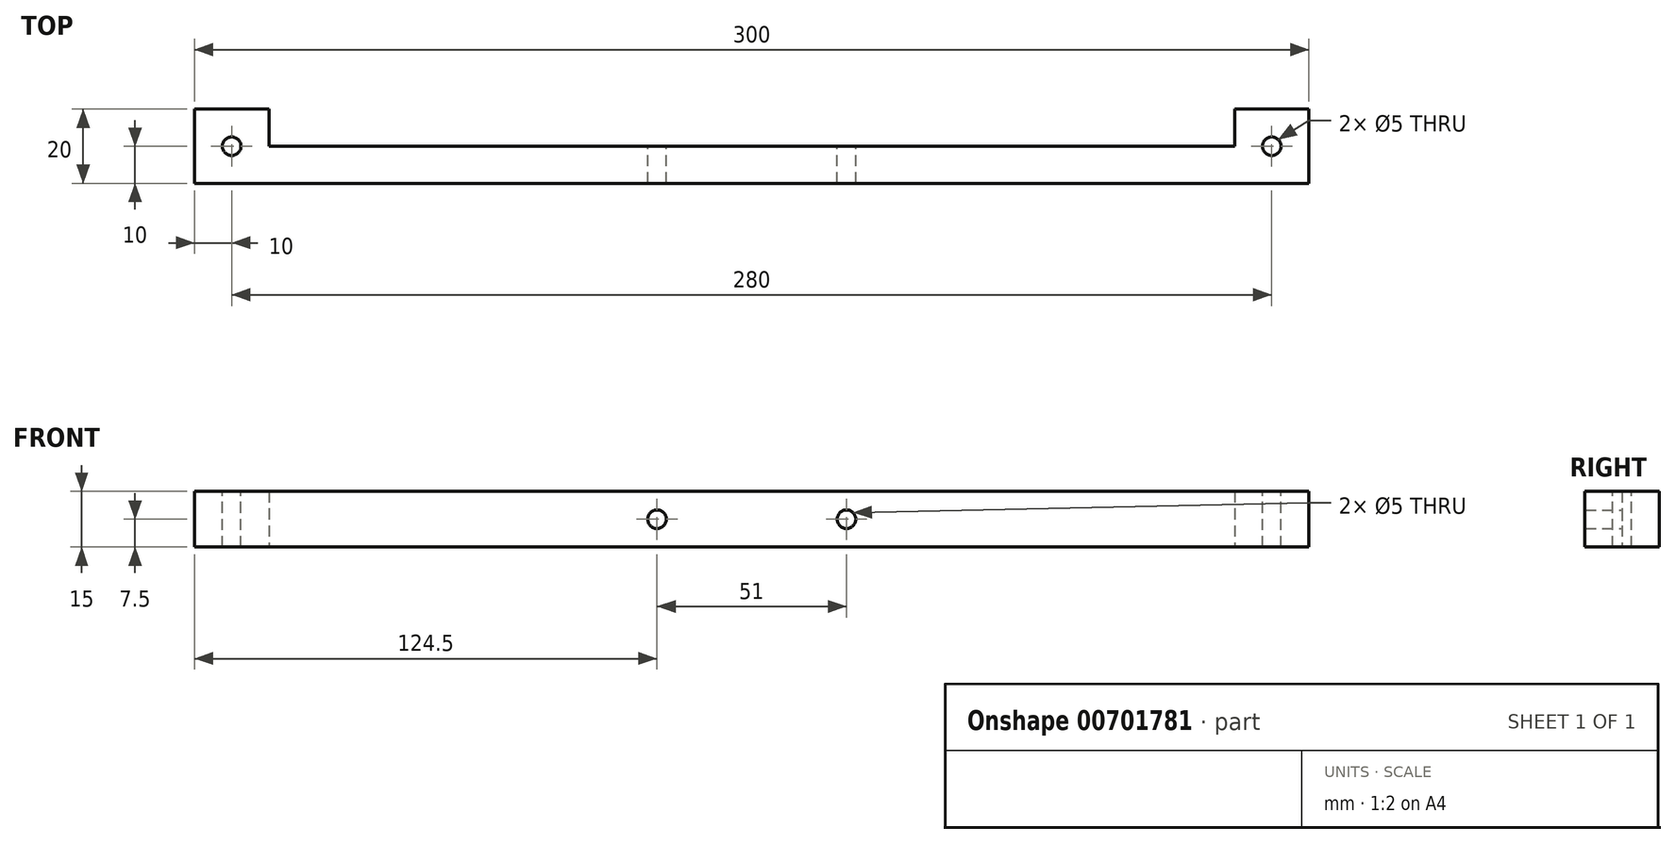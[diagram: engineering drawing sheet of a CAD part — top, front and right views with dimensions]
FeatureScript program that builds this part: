
annotation { "Feature Type Name" : "Feature", "Feature Type Description" : "" }
export const myFeature = defineFeature(function(context is Context, id is Id, definition is map)
    precondition{}
    {
        {
            var Q0;
            Q0=qCreatedBy(makeId("Front.planeOp"),FACE);
            var sketch = newSketch(context, id + "F0", { "sketchPlane" : qUnion([Q0])});
            skLineSegment(sketch, "E0.bottom", {"start": v(-150, 7.5) * mm, "end": v(150, 7.5) * mm});
            skLineSegment(sketch, "E0.top", {"start": v(-150, -7.5) * mm, "end": v(150, -7.5) * mm});
            skLineSegment(sketch, "E0.left", {"start": v(-150, 7.5) * mm, "end": v(-150, -7.5) * mm});
            skLineSegment(sketch, "E0.right", {"start": v(150, 7.5) * mm, "end": v(150, -7.5) * mm});
            skPoint(sketch, "E0.middle", {"position": v(0, 0) * mm});
            skSolve(sketch);
        }
        {
            var Q0;
            Q0 = qSketchRegion(id + "F0", true);
            extrude(context, id + "F1", {"entities" : qUnion([Q0]), "depth" : 10 * mm, "offsetDistance" : 25 * mm});
        }
        {
            var Q0;
            Q0=makeQuery(id+"F1.opExtrude","CAP_FACE",FACE,{"disambiguationData":[OSD([sQuery(id+"F0.wireOp",EDGE,"E0.bottom"),sQuery(id+"F0.wireOp",EDGE,"E0.top"),sQuery(id+"F0.wireOp",EDGE,"E0.left"),sQuery(id+"F0.wireOp",EDGE,"E0.right")])],"isStart":true});
            var sketch = newSketch(context, id + "F2", { "sketchPlane" : qUnion([Q0])});
            skLineSegment(sketch, "E1.bottom", {"start": v(-150, 7.5) * mm, "end": v(-130, 7.5) * mm});
            skLineSegment(sketch, "E1.top", {"start": v(-150, -7.5) * mm, "end": v(-130, -7.5) * mm});
            skLineSegment(sketch, "E1.left", {"start": v(-150, 7.5) * mm, "end": v(-150, -7.5) * mm});
            skLineSegment(sketch, "E1.right", {"start": v(-130, 7.5) * mm, "end": v(-130, -7.5) * mm});
            skLineSegment(sketch, "E2.bottom", {"start": v(150, 7.5) * mm, "end": v(130, 7.5) * mm});
            skLineSegment(sketch, "E2.top", {"start": v(150, -7.5) * mm, "end": v(130, -7.5) * mm});
            skLineSegment(sketch, "E2.left", {"start": v(150, 7.5) * mm, "end": v(150, -7.5) * mm});
            skLineSegment(sketch, "E2.right", {"start": v(130, 7.5) * mm, "end": v(130, -7.5) * mm});
            skSolve(sketch);
        }
        {
            var Q0;
            Q0 = qSketchRegion(id + "F2", true);
            extrude(context, id + "F3", {"entities" : qUnion([Q0]), "operationType" : NewBodyOperationType.ADD, "depth" : 10 * mm, "offsetDistance" : 25 * mm});
        }
        {
            var Q0;
            Q0=makeQuery(id+"F3.boolean.opBoolean","MERGE",FACE,{"derivedFrom":[makeQuery(id+"F1.opExtrude","SWEPT_FACE",FACE,{"disambiguationData":[OSD([sQuery(id+"F0.wireOp",EDGE,"E0.bottom")])]}),makeQuery(id+"F3.opExtrude","SWEPT_FACE",FACE,{"disambiguationData":[OSD([sQuery(id+"F2.wireOp",EDGE,"E1.bottom")])]}),makeQuery(id+"F3.opExtrude","SWEPT_FACE",FACE,{"disambiguationData":[OSD([sQuery(id+"F2.wireOp",EDGE,"E2.bottom")])]})]});
            var sketch = newSketch(context, id + "F4", { "sketchPlane" : qUnion([Q0])});
            skCircle(sketch, "E3", {"center": v(140, 0) * mm, "radius": 2.5 * mm});
            skCircle(sketch, "E4", {"center": v(-140, 0) * mm, "radius": 2.5 * mm});
            skSolve(sketch);
        }
        {
            var Q0;
            Q0 = qSketchRegion(id + "F4", true);
            extrude(context, id + "F5", {"entities" : qUnion([Q0]), "operationType" : NewBodyOperationType.REMOVE, "oppositeDirection" : true, "depth" : 25 * mm, "offsetDistance" : 25 * mm});
        }
        {
            var Q0;
            Q0=makeQuery(id+"F1.opExtrude","CAP_FACE",FACE,{"disambiguationData":[OSD([sQuery(id+"F0.wireOp",EDGE,"E0.bottom"),sQuery(id+"F0.wireOp",EDGE,"E0.top"),sQuery(id+"F0.wireOp",EDGE,"E0.left"),sQuery(id+"F0.wireOp",EDGE,"E0.right")])],"isStart":true});
            var sketch = newSketch(context, id + "F6", { "sketchPlane" : qUnion([Q0])});
            skCircle(sketch, "E5", {"center": v(-25.5, 0) * mm, "radius": 2.5 * mm});
            skCircle(sketch, "E6", {"center": v(25.5, 0) * mm, "radius": 2.5 * mm});
            skSolve(sketch);
        }
        {
            var Q0;
            Q0 = qSketchRegion(id + "F6", true);
            extrude(context, id + "F7", {"entities" : qUnion([Q0]), "operationType" : NewBodyOperationType.REMOVE, "oppositeDirection" : true, "depth" : 25 * mm, "offsetDistance" : 25 * mm});
        }
    });
